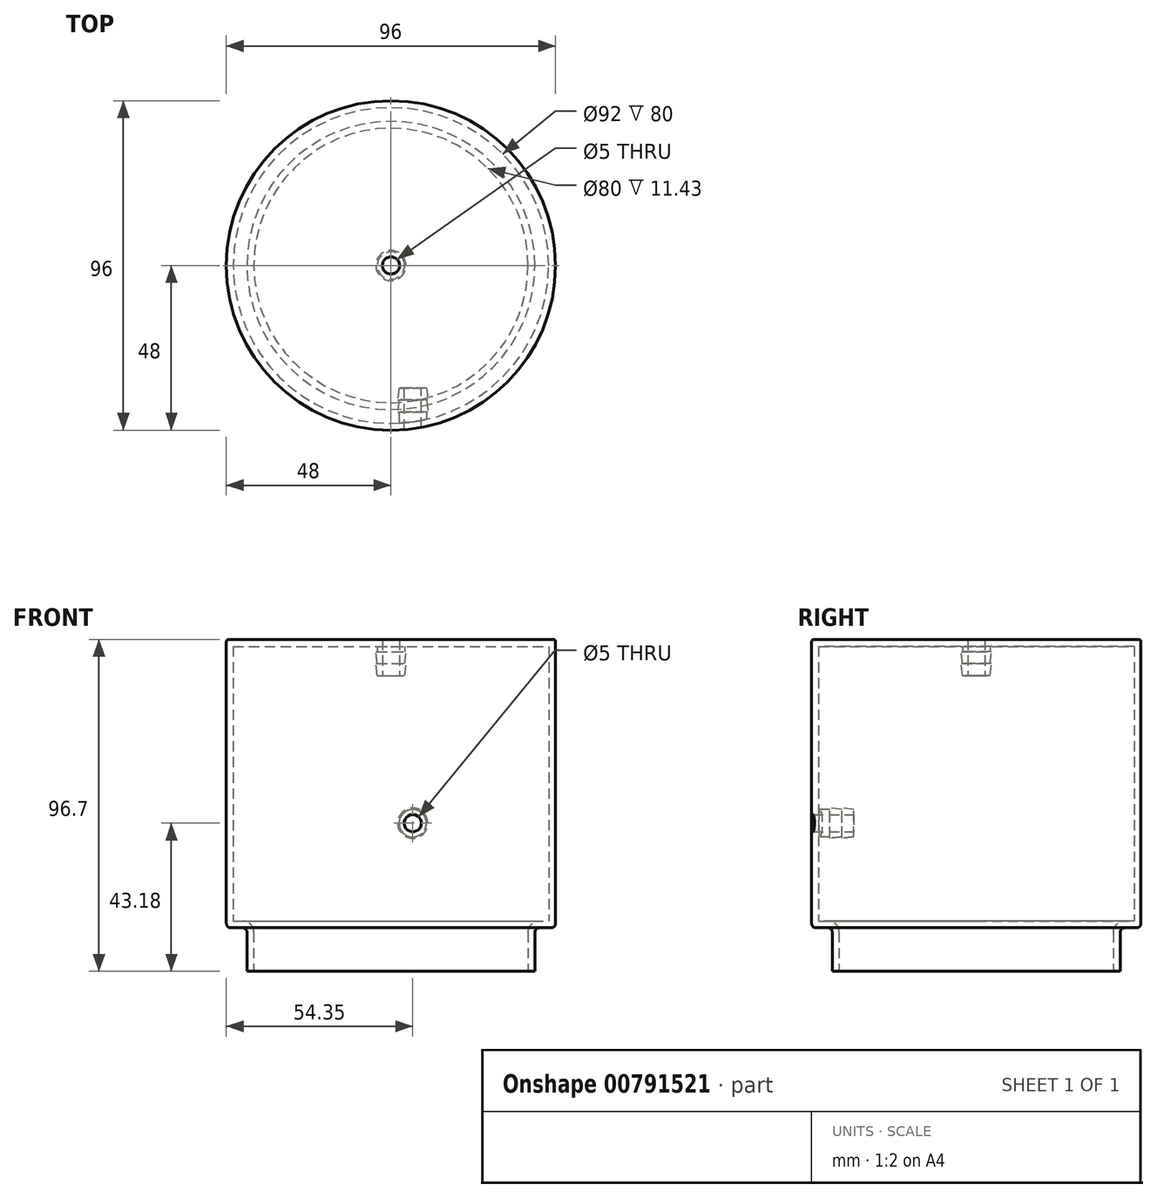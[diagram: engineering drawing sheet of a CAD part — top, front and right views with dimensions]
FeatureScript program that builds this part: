
annotation { "Feature Type Name" : "Feature", "Feature Type Description" : "" }
export const myFeature = defineFeature(function(context is Context, id is Id, definition is map)
    precondition{}
    {
        {
            var Q0;
            Q0=qCreatedBy(makeId("Front.planeOp"),FACE);
            var sketch = newSketch(context, id + "F0", { "sketchPlane" : qUnion([Q0])});
            skLineSegment(sketch, "E0", {"start": v(-42, 0) * mm, "end": v(-42, 11.43) * mm});
            skLineSegment(sketch, "E1", {"start": v(-43.27, 12.7) * mm, "end": v(-46.73, 12.7) * mm});
            skLineSegment(sketch, "E2", {"start": v(-48, 13.97) * mm, "end": v(-48, 96.07) * mm});
            skLineSegment(sketch, "E3", {"start": v(-47.37, 96.7) * mm, "end": v(-2.5, 96.7) * mm});
            skLineSegment(sketch, "E4", {"start": v(-4, 94.7) * mm, "end": v(-4, 93.2) * mm});
            skLineSegment(sketch, "E5.0", {"start": v(-2.5, 96.7) * mm, "end": v(-2.5, 86.2) * mm});
            skLineSegment(sketch, "E6", {"start": v(-4, 93.2) * mm, "end": v(-4.4, 93.2) * mm});
            skLineSegment(sketch, "E7", {"start": v(-4.4, 93.2) * mm, "end": v(-4, 89.7) * mm});
            skLineSegment(sketch, "E8", {"start": v(-4, 89.7) * mm, "end": v(-4.4, 89.7) * mm});
            skLineSegment(sketch, "E9", {"start": v(-4.4, 89.7) * mm, "end": v(-4, 86.2) * mm});
            skLineSegment(sketch, "E10", {"start": v(-4, 86.2) * mm, "end": v(-2.5, 86.2) * mm});
            skPoint(sketch, "E11.visualSharp", {"position": v(-48, 96.7) * mm});
            skArc(sketch, "E11.filletArc", {"start": v(-47.37, 96.7) * mm, "mid": v(-47.81, 96.51) * mm, "end": v(-48, 96.07) * mm});
            skPoint(sketch, "E12.visualSharp", {"position": v(-48, 12.7) * mm});
            skArc(sketch, "E12.filletArc", {"start": v(-48, 13.97) * mm, "mid": v(-47.63, 13.07) * mm, "end": v(-46.73, 12.7) * mm});
            skPoint(sketch, "E13.visualSharp", {"position": v(-42, 12.7) * mm});
            skArc(sketch, "E13.filletArc", {"start": v(-42, 11.43) * mm, "mid": v(-42.37, 12.33) * mm, "end": v(-43.27, 12.7) * mm});
            skLineSegment(sketch, "E14.0", {"start": v(-46, 94.7) * mm, "end": v(-4, 94.7) * mm});
            skLineSegment(sketch, "E14.1", {"start": v(-40, 0) * mm, "end": v(-40, 11.43) * mm});
            skArc(sketch, "E14.2", {"start": v(-40, 11.43) * mm, "mid": v(-40.96, 13.74) * mm, "end": v(-43.27, 14.7) * mm});
            skLineSegment(sketch, "E14.3", {"start": v(-43.27, 14.7) * mm, "end": v(-46, 14.7) * mm});
            skLineSegment(sketch, "E14.4", {"start": v(-46, 14.7) * mm, "end": v(-46, 94.7) * mm});
            skLineSegment(sketch, "E15", {"start": v(-42, 0) * mm, "end": v(-40, 0) * mm});
            skSolve(sketch);
        }
        {
            var Q0;
            Q0=qCreatedBy(makeId("Front.planeOp"),FACE);
            var sketch = newSketch(context, id + "F1", { "sketchPlane" : qUnion([Q0])});
            skLineSegment(sketch, "E16", {"start": v(0, 0) * mm, "end": v(0, 103.69) * mm, "construction": true});
            skSolve(sketch);
        }
        {
            var Q0;
            Q0 = qSketchRegion(id + "F0", true);
            var Q1;
            Q1=sQuery(id+"F1.wireOp",EDGE,"E16");
            revolve(context, id + "F2", {"surfaceOperationType" : NewSurfaceOperationType.NEW, "entities" : qUnion([Q0]), "axis" : qUnion([Q1]), "revolveType" : RevolveType.FULL});
        }
        {
            var Q0;
            Q0=qCreatedBy(makeId("Front.planeOp"),FACE);
            var sketch = newSketch(context, id + "F3", { "sketchPlane" : qUnion([Q0])});
            skCircle(sketch, "E17", {"center": v(6.35, 43.18) * mm, "radius": 2.5 * mm});
            skSolve(sketch);
        }
        {
            var Q0;
            Q0 = qSketchRegion(id + "F3", true);
            extrude(context, id + "F4", {"entities" : qUnion([Q0]), "operationType" : NewBodyOperationType.REMOVE, "depth" : 76.2 * mm, "offsetDistance" : 25.4 * mm});
        }
        {
            var Q0;
            Q0=qCreatedBy(makeId("Right.planeOp"),FACE);
            cPlane(context, id + "F5", {"entities" : qUnion([Q0]), "cplaneType" : CPlaneType.OFFSET, "offset" : 6.35 * mm, "width" : 152.4 * mm, "height" : 152.4 * mm});
        }
        {
            var Q0;
            Q0=qCreatedBy(id+"F5.planeOp",FACE);
            var sketch = newSketch(context, id + "F6", { "sketchPlane" : qUnion([Q0])});
            skLineSegment(sketch, "E18", {"start": v(-39.23, 43.18) * mm, "end": v(6.21, 43.18) * mm, "construction": true});
            skSolve(sketch);
        }
        {
            var Q0;
            Q0=qCreatedBy(id+"F5.planeOp",FACE);
            var sketch = newSketch(context, id + "F7", { "sketchPlane" : qUnion([Q0])});
            skLineSegment(sketch, "E19.0", {"start": v(-39.23, 43.18) * mm, "end": v(6.21, 43.18) * mm, "construction": true});
            skLineSegment(sketch, "E20.0", {"start": v(-46.2, 47.18) * mm, "end": v(10.22, 47.18) * mm});
            skLineSegment(sketch, "E21.0", {"start": v(-46.2, 45.68) * mm, "end": v(10.22, 45.68) * mm});
            skLineSegment(sketch, "E22", {"start": v(-46.2, 48.33) * mm, "end": v(-46.2, 44.59) * mm});
            skLineSegment(sketch, "E23.0", {"start": v(-42.7, 47.58) * mm, "end": v(-42.7, 47.18) * mm});
            skLineSegment(sketch, "E24", {"start": v(-42.7, 47.58) * mm, "end": v(-39.2, 47.18) * mm});
            skLineSegment(sketch, "E25", {"start": v(-39.2, 47.18) * mm, "end": v(-39.2, 47.58) * mm});
            skLineSegment(sketch, "E26", {"start": v(-39.2, 47.58) * mm, "end": v(-35.7, 47.18) * mm});
            skLineSegment(sketch, "E27", {"start": v(-35.7, 47.18) * mm, "end": v(-35.7, 45.68) * mm});
            skSolve(sketch);
        }
        {
            var Q0;
            Q0 = qSketchRegion(id + "F7", true);
            var Q1;
            Q1=sQuery(id+"F7.wireOp",EDGE,"E19.0");
            revolve(context, id + "F8", {"operationType" : NewBodyOperationType.ADD, "surfaceOperationType" : NewSurfaceOperationType.NEW, "entities" : qUnion([Q0]), "axis" : qUnion([Q1]), "revolveType" : RevolveType.FULL});
        }
    });
